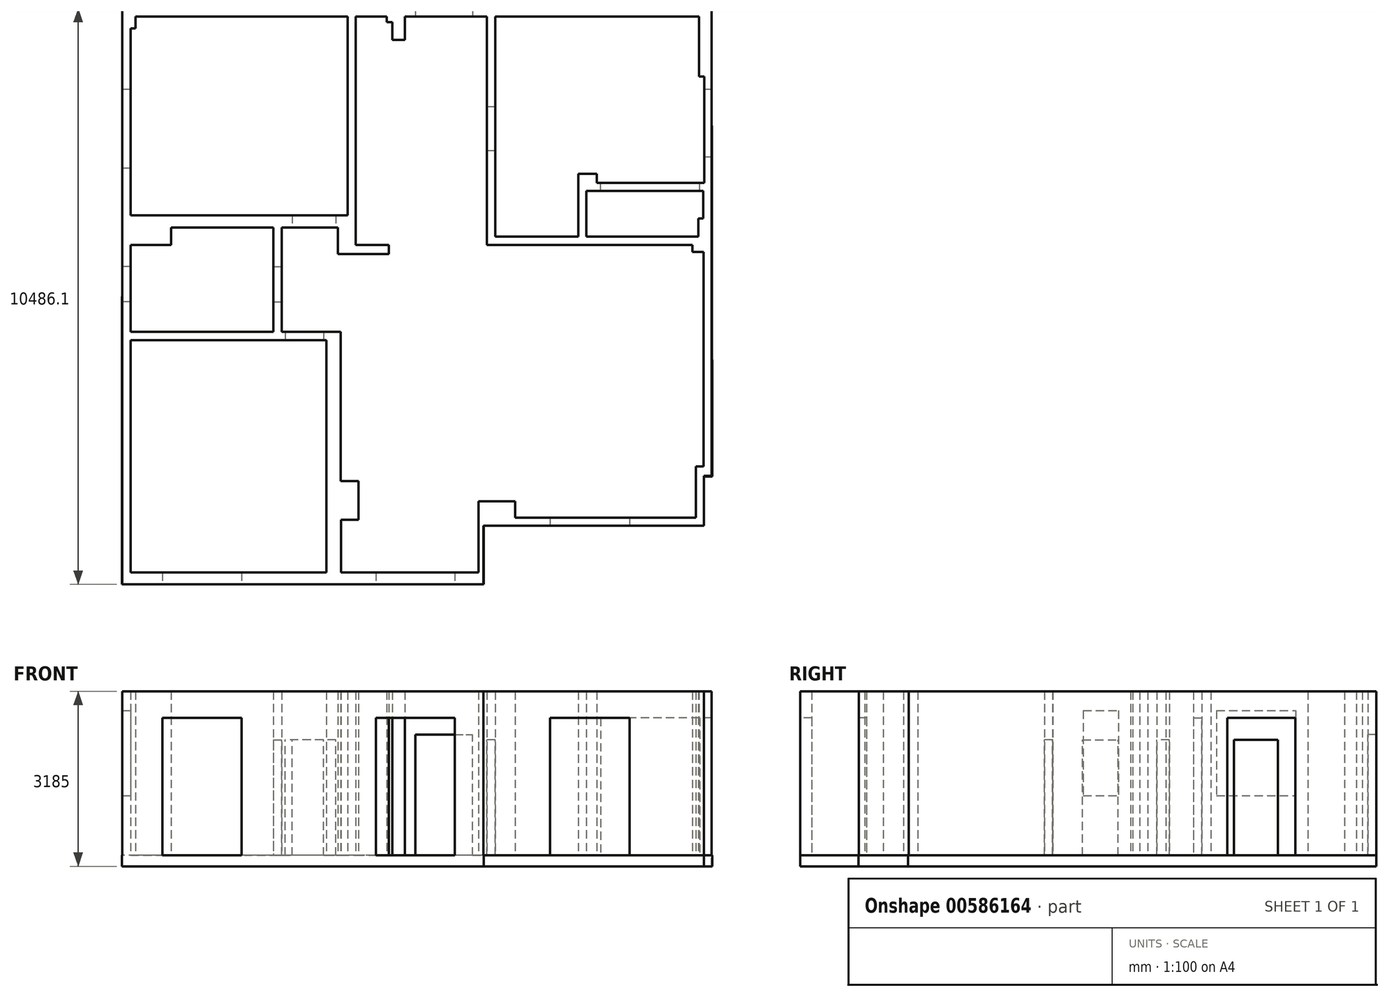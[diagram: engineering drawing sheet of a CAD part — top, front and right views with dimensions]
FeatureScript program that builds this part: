
annotation { "Feature Type Name" : "Feature", "Feature Type Description" : "" }
export const myFeature = defineFeature(function(context is Context, id is Id, definition is map)
    precondition{}
    {
        {
            var Q0;
            Q0=qCreatedBy(makeId("Top.planeOp"),FACE);
            var sketch = newSketch(context, id + "F0", { "sketchPlane" : qUnion([Q0])});
            skLineSegment(sketch, "E0", {"start": v(264.38, 0) * mm, "end": v(4001, 0) * mm});
            skLineSegment(sketch, "E1", {"start": v(4001, 0) * mm, "end": v(4001, -125) * mm});
            skLineSegment(sketch, "E2", {"start": v(4001, -125) * mm, "end": v(4202.95, -125) * mm});
            skLineSegment(sketch, "E3", {"start": v(4202.95, -125) * mm, "end": v(4202.95, -4036) * mm});
            skLineSegment(sketch, "E4", {"start": v(4202.95, -4036) * mm, "end": v(4062.95, -4036) * mm});
            skLineSegment(sketch, "E5", {"start": v(4062.95, -4036) * mm, "end": v(4062.95, -4967) * mm});
            skLineSegment(sketch, "E6", {"start": v(4062.95, -4967) * mm, "end": v(2970.95, -4967) * mm});
            skLineSegment(sketch, "E7", {"start": v(2970.95, -4967) * mm, "end": v(1520.95, -4967) * mm});
            skLineSegment(sketch, "E8", {"start": v(1520.95, -4967) * mm, "end": v(778.95, -4967) * mm});
            skLineSegment(sketch, "E9", {"start": v(778.95, -4967) * mm, "end": v(778.95, -4667) * mm});
            skLineSegment(sketch, "E10", {"start": v(778.95, -4667) * mm, "end": v(106.95, -4667) * mm});
            skLineSegment(sketch, "E11", {"start": v(106.95, -4667) * mm, "end": v(106.95, -5966) * mm});
            skLineSegment(sketch, "E12", {"start": v(106.95, -5966) * mm, "end": v(-320.05, -5966) * mm});
            skLineSegment(sketch, "E13", {"start": v(-320.05, -5966) * mm, "end": v(-1760.05, -5966) * mm});
            skLineSegment(sketch, "E14", {"start": v(-1760.05, -5966) * mm, "end": v(-2394.05, -5966) * mm});
            skLineSegment(sketch, "E15", {"start": v(-2394.05, -5966) * mm, "end": v(-2394.05, -5002) * mm});
            skLineSegment(sketch, "E16", {"start": v(-2394.05, -5002) * mm, "end": v(-2075.05, -5002) * mm});
            skLineSegment(sketch, "E17", {"start": v(-2075.05, -5002) * mm, "end": v(-2075.05, -4297) * mm});
            skLineSegment(sketch, "E18", {"start": v(-2075.05, -4297) * mm, "end": v(-2399.05, -4297) * mm});
            skLineSegment(sketch, "E19", {"start": v(-2399.05, -4297) * mm, "end": v(-2399.05, -1583) * mm});
            skLineSegment(sketch, "E20.19", {"start": v(3945.9, -4961.9) * mm, "end": v(2859, -4961.9) * mm});
            skLineSegment(sketch, "E21.0", {"start": v(2800.47, -5111.9) * mm, "end": v(1350.47, -5111.9) * mm});
            skLineSegment(sketch, "E22.0", {"start": v(1409, -5111.9) * mm, "end": v(720.85, -5111.9) * mm});
            skLineSegment(sketch, "E23", {"start": v(720.85, -5111.9) * mm, "end": v(198.85, -5111.9) * mm});
            skLineSegment(sketch, "E24", {"start": v(198.85, -5111.9) * mm, "end": v(198.85, -6179.3) * mm});
            skLineSegment(sketch, "E25", {"start": v(-435.2, -6179.3) * mm, "end": v(198.85, -6179.3) * mm});
            skLineSegment(sketch, "E26", {"start": v(2800.47, -5111.9) * mm, "end": v(4212.95, -5111.9) * mm});
            skLineSegment(sketch, "E27", {"start": v(-435.2, -6179.3) * mm, "end": v(-1872, -6179.3) * mm});
            skLineSegment(sketch, "E28", {"start": v(-1872, -6179.3) * mm, "end": v(-2660.9, -6179.3) * mm});
            skLineSegment(sketch, "E29", {"start": v(-2660.9, -1733) * mm, "end": v(-2660.9, -5966) * mm});
            skLineSegment(sketch, "E30", {"start": v(-2660.9, -1583) * mm, "end": v(-2399.05, -1583) * mm});
            skLineSegment(sketch, "E31", {"start": v(-1227.62, 4156.8) * mm, "end": v(-1227.62, 3731.8) * mm});
            skLineSegment(sketch, "E32", {"start": v(-1227.62, 3731.8) * mm, "end": v(-1461.62, 3731.8) * mm});
            skLineSegment(sketch, "E33", {"start": v(-1461.62, 3731.8) * mm, "end": v(-1461.62, 4055.8) * mm});
            skLineSegment(sketch, "E34", {"start": v(-1461.62, 4055.8) * mm, "end": v(-1562.62, 4055.8) * mm});
            skLineSegment(sketch, "E35", {"start": v(-1562.62, 4055.8) * mm, "end": v(-1562.62, 4156.8) * mm});
            skLineSegment(sketch, "E36", {"start": v(-1562.62, 4156.8) * mm, "end": v(-2123.62, 4156.8) * mm});
            skLineSegment(sketch, "E37", {"start": v(-2123.62, 4156.8) * mm, "end": v(-2123.62, 150) * mm});
            skLineSegment(sketch, "E38", {"start": v(264.38, 4156.8) * mm, "end": v(264.38, 0) * mm});
            skLineSegment(sketch, "E39", {"start": v(-1227.62, 4156.8) * mm, "end": v(264.38, 4156.8) * mm});
            skLineSegment(sketch, "E40.0", {"start": v(4198.9, 479.37) * mm, "end": v(4198.9, 981.37) * mm});
            skLineSegment(sketch, "E41", {"start": v(4108.9, 479.37) * mm, "end": v(4108.9, 149.4) * mm});
            skLineSegment(sketch, "E42", {"start": v(4108.9, 479.37) * mm, "end": v(4198.9, 479.37) * mm});
            skLineSegment(sketch, "E43", {"start": v(2073.52, 981.37) * mm, "end": v(4198.9, 981.37) * mm});
            skLineSegment(sketch, "E44.0", {"start": v(2262.52, 1131.37) * mm, "end": v(4215.38, 1131.37) * mm});
            skLineSegment(sketch, "E45", {"start": v(2262.52, 1131.37) * mm, "end": v(2262.52, 1296.37) * mm});
            skLineSegment(sketch, "E46", {"start": v(2262.52, 1296.37) * mm, "end": v(1923.52, 1296.37) * mm});
            skLineSegment(sketch, "E47.0", {"start": v(414.38, 4156.8) * mm, "end": v(414.38, 1131.37) * mm});
            skLineSegment(sketch, "E48", {"start": v(-2273.62, 4306.8) * mm, "end": v(4352.95, 4306.8) * mm});
            skLineSegment(sketch, "E49", {"start": v(414.38, 4156.8) * mm, "end": v(4125.38, 4156.8) * mm});
            skLineSegment(sketch, "E50.trimOffspring", {"start": v(4125.38, 4156.8) * mm, "end": v(4125.38, 3063.8) * mm});
            skLineSegment(sketch, "E51", {"start": v(2259.9, 150) * mm, "end": v(2259.9, 149.78) * mm});
            skLineSegment(sketch, "E52", {"start": v(2073.52, 149.82) * mm, "end": v(4108.9, 149.4) * mm});
            skLineSegment(sketch, "E53.trimOffspring", {"start": v(414.38, 1131.37) * mm, "end": v(414.38, 150) * mm});
            skLineSegment(sketch, "E54", {"start": v(-2273.62, 4156.8) * mm, "end": v(-2273.62, 541.1) * mm});
            skLineSegment(sketch, "E55.trimOffspring", {"start": v(414.38, 150) * mm, "end": v(1923.52, 150) * mm});
            skLineSegment(sketch, "E56", {"start": v(-2123.62, 150) * mm, "end": v(-2123.62, 0) * mm});
            skLineSegment(sketch, "E57", {"start": v(-2123.62, -166) * mm, "end": v(-2448.62, -166) * mm});
            skLineSegment(sketch, "E58", {"start": v(-2448.62, -166) * mm, "end": v(-2448.62, 316) * mm});
            skLineSegment(sketch, "E59", {"start": v(-3472.9, 316) * mm, "end": v(-3472.9, -1579.32) * mm});
            skLineSegment(sketch, "E60", {"start": v(-2448.62, 316) * mm, "end": v(-3472.9, 316) * mm});
            skLineSegment(sketch, "E61", {"start": v(-3472.9, -1579.32) * mm, "end": v(-2660.9, -1583) * mm});
            skLineSegment(sketch, "E62", {"start": v(-3622.9, 541.1) * mm, "end": v(-2273.62, 541.1) * mm});
            skLineSegment(sketch, "E63", {"start": v(-3622.9, 316) * mm, "end": v(-3622.9, -1583) * mm});
            skLineSegment(sketch, "E64", {"start": v(-2660.9, -1733) * mm, "end": v(-6222.9, -1733) * mm});
            skLineSegment(sketch, "E65", {"start": v(-6222.9, -1733) * mm, "end": v(-6222.9, -5966) * mm});
            skLineSegment(sketch, "E66", {"start": v(-2394.05, -5966) * mm, "end": v(-6222.9, -5966) * mm});
            skLineSegment(sketch, "E67", {"start": v(-2660.9, -6179.3) * mm, "end": v(-6372.9, -6179.3) * mm});
            skLineSegment(sketch, "E68", {"start": v(-6372.9, 541.1) * mm, "end": v(-6372.9, -6179.3) * mm});
            skLineSegment(sketch, "E69", {"start": v(-3622.9, -1583) * mm, "end": v(-6222.9, -1583) * mm});
            skLineSegment(sketch, "E70", {"start": v(-6222.9, -1583) * mm, "end": v(-6222.9, 0) * mm});
            skLineSegment(sketch, "E71", {"start": v(-3622.9, 316) * mm, "end": v(-5487.9, 316) * mm});
            skLineSegment(sketch, "E72", {"start": v(-5487.9, 316) * mm, "end": v(-5487.9, 0) * mm});
            skLineSegment(sketch, "E73", {"start": v(-6222.9, 0) * mm, "end": v(-5487.9, 0) * mm});
            skLineSegment(sketch, "E74", {"start": v(-3622.9, 541.1) * mm, "end": v(-6222.9, 541.1) * mm});
            skLineSegment(sketch, "E75", {"start": v(-6372.9, 541.1) * mm, "end": v(-6372.9, 4306.8) * mm});
            skLineSegment(sketch, "E76", {"start": v(-2273.62, 4306.8) * mm, "end": v(-6372.9, 4306.8) * mm});
            skLineSegment(sketch, "E77", {"start": v(-6222.9, 541.1) * mm, "end": v(-6222.9, 3944.8) * mm});
            skLineSegment(sketch, "E78", {"start": v(-2273.62, 4156.8) * mm, "end": v(-6132.9, 4156.8) * mm});
            skLineSegment(sketch, "E79", {"start": v(-6132.9, 4156.8) * mm, "end": v(-6132.9, 3944.8) * mm});
            skLineSegment(sketch, "E80.trimOffspring", {"start": v(-6222.9, 3944.8) * mm, "end": v(-6132.9, 3944.8) * mm});
            skLineSegment(sketch, "E81", {"start": v(4125.38, 3063.8) * mm, "end": v(4215.38, 3063.8) * mm});
            skLineSegment(sketch, "E82", {"start": v(4215.38, 3063.8) * mm, "end": v(4215.38, 1131.37) * mm});
            skLineSegment(sketch, "E83", {"start": v(4352.95, 4306.8) * mm, "end": v(4352.95, -4204.43) * mm});
            skLineSegment(sketch, "E84", {"start": v(4212.95, -4204.43) * mm, "end": v(4212.95, -5111.9) * mm});
            skLineSegment(sketch, "E85.trimOffspring", {"start": v(4212.95, -4204.43) * mm, "end": v(4352.95, -4204.43) * mm});
            skLineSegment(sketch, "E86", {"start": v(-2123.62, -166) * mm, "end": v(-1523.62, -166) * mm});
            skLineSegment(sketch, "E87", {"start": v(-2123.62, 0) * mm, "end": v(-1523.62, 0) * mm});
            skLineSegment(sketch, "E88", {"start": v(-1523.62, -166) * mm, "end": v(-1523.62, 0) * mm});
            skLineSegment(sketch, "E89", {"start": v(1923.52, 1296.37) * mm, "end": v(1923.52, 150) * mm});
            skLineSegment(sketch, "E90", {"start": v(2073.52, 981.37) * mm, "end": v(2073.52, 145.98) * mm});
            skPoint(sketch, "E91.orphan", {"position": v(2259.9, 981.37) * mm});
            skLineSegment(sketch, "E92", {"start": v(4062.95, -4501.5) * mm, "end": v(912.95, -4501.5) * mm});
            skLineSegment(sketch, "E93", {"start": v(4062.95, -4501.5) * mm, "end": v(4062.95, -2701.5) * mm});
            skLineSegment(sketch, "E94", {"start": v(4062.95, -2701.5) * mm, "end": v(2945.08, -2701.5) * mm});
            skLineSegment(sketch, "E95", {"start": v(2945.08, -2701.5) * mm, "end": v(2945.08, -3501.5) * mm});
            skLineSegment(sketch, "E96", {"start": v(2945.08, -3501.5) * mm, "end": v(869.18, -3501.5) * mm});
            skLineSegment(sketch, "E97", {"start": v(869.18, -3501.5) * mm, "end": v(912.95, -4501.5) * mm});
            skSolve(sketch);
        }
        {
            var Q0;
            Q0=qSketchRegion(id+"F0",true);
            extrude(context, id + "F1", {"entities" : qUnion([Q0]), "depth" : 2985 * mm, "offsetDistance" : 25 * mm});
        }
        {
            var Q0;
            Q0=makeQuery(id+"F1.opExtrude","SWEPT_FACE",FACE,{"disambiguationData":[OSD([sQuery(id+"F0.wireOp",EDGE,"E21.0"),sQuery(id+"F0.wireOp",EDGE,"E22.0"),sQuery(id+"F0.wireOp",EDGE,"E23"),sQuery(id+"F0.wireOp",EDGE,"E26")])]});
            var sketch = newSketch(context, id + "F2", { "sketchPlane" : qUnion([Q0])});
            skLineSegment(sketch, "E98.bottom", {"start": v(2859, 0) * mm, "end": v(1409, 0) * mm});
            skLineSegment(sketch, "E98.top", {"start": v(2859, 2500) * mm, "end": v(1409, 2500) * mm});
            skLineSegment(sketch, "E98.left", {"start": v(2859, 0) * mm, "end": v(2859, 2500) * mm});
            skLineSegment(sketch, "E98.right", {"start": v(1409, 0) * mm, "end": v(1409, 2500) * mm});
            skSolve(sketch);
        }
        {
            var Q0;
            Q0=qSketchRegion(id+"F2",true);
            extrude(context, id + "F3", {"entities" : qUnion([Q0]), "operationType" : NewBodyOperationType.REMOVE, "endBound" : BoundingType.UP_TO_NEXT, "oppositeDirection" : true, "depth" : 25 * mm, "offsetDistance" : 25 * mm});
        }
        {
            var Q0;
            Q0=makeQuery(id+"F1.opExtrude","SWEPT_FACE",FACE,{"disambiguationData":[OSD([sQuery(id+"F0.wireOp",EDGE,"E25"),sQuery(id+"F0.wireOp",EDGE,"E27"),sQuery(id+"F0.wireOp",EDGE,"E28"),sQuery(id+"F0.wireOp",EDGE,"E67")])]});
            var sketch = newSketch(context, id + "F4", { "sketchPlane" : qUnion([Q0])});
            skLineSegment(sketch, "E99.bottom", {"start": v(-320.05, 0) * mm, "end": v(-1760.05, 0) * mm});
            skLineSegment(sketch, "E99.top", {"start": v(-320.05, 2500) * mm, "end": v(-1760.05, 2500) * mm});
            skLineSegment(sketch, "E99.left", {"start": v(-320.05, 0) * mm, "end": v(-320.05, 2500) * mm});
            skLineSegment(sketch, "E99.right", {"start": v(-1760.05, 0) * mm, "end": v(-1760.05, 2500) * mm});
            skSolve(sketch);
        }
        {
            var Q0;
            Q0=qSketchRegion(id+"F4",true);
            extrude(context, id + "F5", {"entities" : qUnion([Q0]), "operationType" : NewBodyOperationType.REMOVE, "endBound" : BoundingType.UP_TO_NEXT, "oppositeDirection" : true, "depth" : 25 * mm, "offsetDistance" : 25 * mm});
        }
        {
            var Q0;
            Q0=makeQuery(id+"F1.opExtrude","SWEPT_FACE",FACE,{"disambiguationData":[OSD([sQuery(id+"F0.wireOp",EDGE,"E25"),sQuery(id+"F0.wireOp",EDGE,"E27"),sQuery(id+"F0.wireOp",EDGE,"E28"),sQuery(id+"F0.wireOp",EDGE,"E67")])]});
            var sketch = newSketch(context, id + "F6", { "sketchPlane" : qUnion([Q0])});
            skLineSegment(sketch, "E100.bottom", {"start": v(-4201.9, 0) * mm, "end": v(-5644.9, 0) * mm});
            skLineSegment(sketch, "E100.top", {"start": v(-4201.9, 2500) * mm, "end": v(-5644.9, 2500) * mm});
            skLineSegment(sketch, "E100.left", {"start": v(-4201.9, 0) * mm, "end": v(-4201.9, 2500) * mm});
            skLineSegment(sketch, "E100.right", {"start": v(-5644.9, 0) * mm, "end": v(-5644.9, 2500) * mm});
            skSolve(sketch);
        }
        {
            var Q0;
            Q0=qSketchRegion(id+"F6",true);
            extrude(context, id + "F7", {"entities" : qUnion([Q0]), "operationType" : NewBodyOperationType.REMOVE, "endBound" : BoundingType.UP_TO_NEXT, "oppositeDirection" : true, "depth" : 25 * mm, "offsetDistance" : 25 * mm});
        }
        {
            var Q0;
            Q0=makeQuery(id+"F1.opExtrude","SWEPT_FACE",FACE,{"disambiguationData":[OSD([sQuery(id+"F0.wireOp",EDGE,"E0"),sQuery(id+"F0.wireOp",EDGE,"s7OnHrYy-Djpp-lhPn-glBJ-n8gcuGNVqWHS"),sQuery(id+"F0.wireOp",EDGE,"TmqLxYyP-QGwx-pu5G-LCv3-DPf7TJavojwj")])]});
            var sketch = newSketch(context, id + "F8", { "sketchPlane" : qUnion([Q0])});
            skLineSegment(sketch, "E101.bottom", {"start": v(0, 0) * mm, "end": v(-797, 0) * mm});
            skLineSegment(sketch, "E101.top", {"start": v(0, 2500) * mm, "end": v(-797, 2500) * mm});
            skLineSegment(sketch, "E101.left", {"start": v(0, 0) * mm, "end": v(0, 2500) * mm});
            skLineSegment(sketch, "E101.right", {"start": v(-797, 0) * mm, "end": v(-797, 2500) * mm});
            skSolve(sketch);
        }
        {
            var Q0;
            Q0=qSketchRegion(id+"F8",true);
            extrude(context, id + "F9", {"entities" : qUnion([Q0]), "operationType" : NewBodyOperationType.REMOVE, "endBound" : BoundingType.UP_TO_NEXT, "oppositeDirection" : true, "depth" : 25 * mm, "offsetDistance" : 25 * mm});
        }
        {
            var Q0;
            Q0=makeQuery(id+"F1.opExtrude","SWEPT_FACE",FACE,{"disambiguationData":[OSD([sQuery(id+"F0.wireOp",EDGE,"E38")])]});
            var sketch = newSketch(context, id + "F10", { "sketchPlane" : qUnion([Q0])});
            skLineSegment(sketch, "E102.bottom", {"start": v(-1715.5, 0) * mm, "end": v(-2515.5, 0) * mm});
            skLineSegment(sketch, "E102.top", {"start": v(-1715.5, 2100) * mm, "end": v(-2515.5, 2100) * mm});
            skLineSegment(sketch, "E102.left", {"start": v(-1715.5, 0) * mm, "end": v(-1715.5, 2100) * mm});
            skLineSegment(sketch, "E102.right", {"start": v(-2515.5, 0) * mm, "end": v(-2515.5, 2100) * mm});
            skSolve(sketch);
        }
        {
            var Q0;
            Q0=qSketchRegion(id+"F10",true);
            extrude(context, id + "F11", {"entities" : qUnion([Q0]), "operationType" : NewBodyOperationType.REMOVE, "endBound" : BoundingType.UP_TO_NEXT, "oppositeDirection" : true, "depth" : 25 * mm, "offsetDistance" : 25 * mm});
        }
        {
            var Q0;
            Q0=makeQuery(id+"F1.opExtrude","SWEPT_FACE",FACE,{"disambiguationData":[OSD([sQuery(id+"F0.wireOp",EDGE,"E39")])]});
            var sketch = newSketch(context, id + "F12", { "sketchPlane" : qUnion([Q0])});
            skLineSegment(sketch, "E103.bottom", {"start": v(-1042, 0) * mm, "end": v(0, 0) * mm});
            skLineSegment(sketch, "E103.top", {"start": v(-1042, 2200) * mm, "end": v(0, 2200) * mm});
            skLineSegment(sketch, "E103.left", {"start": v(-1042, 0) * mm, "end": v(-1042, 2200) * mm});
            skLineSegment(sketch, "E103.right", {"start": v(0, 0) * mm, "end": v(0, 2200) * mm});
            skSolve(sketch);
        }
        {
            var Q0;
            Q0=qSketchRegion(id+"F12",true);
            extrude(context, id + "F13", {"entities" : qUnion([Q0]), "operationType" : NewBodyOperationType.REMOVE, "endBound" : BoundingType.UP_TO_NEXT, "oppositeDirection" : true, "depth" : 25 * mm, "offsetDistance" : 25 * mm});
        }
        {
            var Q0;
            Q0=makeQuery(id+"F1.opExtrude","SWEPT_FACE",FACE,{"disambiguationData":[OSD([sQuery(id+"F0.wireOp",EDGE,"E82")])]});
            var sketch = newSketch(context, id + "F14", { "sketchPlane" : qUnion([Q0])});
            skLineSegment(sketch, "E104.bottom", {"start": v(-2833.8, 0) * mm, "end": v(-1598.8, 0) * mm});
            skLineSegment(sketch, "E104.top", {"start": v(-2833.8, 2500) * mm, "end": v(-1598.8, 2500) * mm});
            skLineSegment(sketch, "E104.left", {"start": v(-2833.8, 0) * mm, "end": v(-2833.8, 2500) * mm});
            skLineSegment(sketch, "E104.right", {"start": v(-1598.8, 0) * mm, "end": v(-1598.8, 2500) * mm});
            skSolve(sketch);
        }
        {
            var Q0;
            Q0=qSketchRegion(id+"F14",true);
            extrude(context, id + "F15", {"entities" : qUnion([Q0]), "operationType" : NewBodyOperationType.REMOVE, "endBound" : BoundingType.UP_TO_NEXT, "oppositeDirection" : true, "depth" : 25 * mm, "offsetDistance" : 25 * mm});
        }
        {
            var Q0;
            Q0=makeQuery(id+"F1.opExtrude","SWEPT_FACE",FACE,{"disambiguationData":[OSD([sQuery(id+"F0.wireOp",EDGE,"E64")])]});
            var sketch = newSketch(context, id + "F16", { "sketchPlane" : qUnion([Q0])});
            skLineSegment(sketch, "E105.bottom", {"start": v(-2710.9, 0) * mm, "end": v(-3410.9, 0) * mm});
            skLineSegment(sketch, "E105.top", {"start": v(-2710.9, 2100) * mm, "end": v(-3410.9, 2100) * mm});
            skLineSegment(sketch, "E105.left", {"start": v(-2710.9, 0) * mm, "end": v(-2710.9, 2100) * mm});
            skLineSegment(sketch, "E105.right", {"start": v(-3410.9, 0) * mm, "end": v(-3410.9, 2100) * mm});
            skSolve(sketch);
        }
        {
            var Q0;
            Q0=qSketchRegion(id+"F16",true);
            extrude(context, id + "F17", {"entities" : qUnion([Q0]), "operationType" : NewBodyOperationType.REMOVE, "endBound" : BoundingType.UP_TO_NEXT, "oppositeDirection" : true, "depth" : 25 * mm, "offsetDistance" : 25 * mm});
        }
        {
            var Q0;
            Q0=makeQuery(id+"F1.opExtrude","SWEPT_FACE",FACE,{"disambiguationData":[OSD([sQuery(id+"F0.wireOp",EDGE,"E60")])]});
            var sketch = newSketch(context, id + "F18", { "sketchPlane" : qUnion([Q0])});
            skLineSegment(sketch, "E106.bottom", {"start": v(-2488.9, 0) * mm, "end": v(-3282.9, 0) * mm});
            skLineSegment(sketch, "E106.top", {"start": v(-2488.9, 2100) * mm, "end": v(-3282.9, 2100) * mm});
            skLineSegment(sketch, "E106.left", {"start": v(-2488.9, 0) * mm, "end": v(-2488.9, 2100) * mm});
            skLineSegment(sketch, "E106.right", {"start": v(-3282.9, 0) * mm, "end": v(-3282.9, 2100) * mm});
            skSolve(sketch);
        }
        {
            var Q0;
            Q0=qSketchRegion(id+"F18",true);
            extrude(context, id + "F19", {"entities" : qUnion([Q0]), "operationType" : NewBodyOperationType.REMOVE, "endBound" : BoundingType.UP_TO_NEXT, "oppositeDirection" : true, "depth" : 25 * mm, "offsetDistance" : 25 * mm});
        }
        {
            var Q0;
            Q0=makeQuery(id+"F1.opExtrude","SWEPT_FACE",FACE,{"disambiguationData":[OSD([sQuery(id+"F0.wireOp",EDGE,"E59")])]});
            var sketch = newSketch(context, id + "F20", { "sketchPlane" : qUnion([Q0])});
            skLineSegment(sketch, "E107.bottom", {"start": v(-1039, 0) * mm, "end": v(-393, 0) * mm});
            skLineSegment(sketch, "E107.top", {"start": v(-1039, 2100) * mm, "end": v(-393, 2100) * mm});
            skLineSegment(sketch, "E107.left", {"start": v(-1039, 0) * mm, "end": v(-1039, 2100) * mm});
            skLineSegment(sketch, "E107.right", {"start": v(-393, 0) * mm, "end": v(-393, 2100) * mm});
            skSolve(sketch);
        }
        {
            var Q0;
            Q0=qSketchRegion(id+"F20",true);
            extrude(context, id + "F21", {"entities" : qUnion([Q0]), "operationType" : NewBodyOperationType.REMOVE, "endBound" : BoundingType.UP_TO_NEXT, "oppositeDirection" : true, "depth" : 25 * mm, "offsetDistance" : 25 * mm});
        }
        {
            var Q0;
            Q0=makeQuery(id+"F1.opExtrude","SWEPT_FACE",FACE,{"disambiguationData":[OSD([sQuery(id+"F0.wireOp",EDGE,"E70")])]});
            var sketch = newSketch(context, id + "F22", { "sketchPlane" : qUnion([Q0])});
            skLineSegment(sketch, "E108.bottom", {"start": v(-1027.15, 2635) * mm, "end": v(-387.15, 2635) * mm});
            skLineSegment(sketch, "E108.top", {"start": v(-1027.15, 1085) * mm, "end": v(-387.15, 1085) * mm});
            skLineSegment(sketch, "E108.left", {"start": v(-1027.15, 2635) * mm, "end": v(-1027.15, 1085) * mm});
            skLineSegment(sketch, "E108.right", {"start": v(-387.15, 2635) * mm, "end": v(-387.15, 1085) * mm});
            skSolve(sketch);
        }
        {
            var Q0;
            Q0=qSketchRegion(id+"F22",true);
            extrude(context, id + "F23", {"entities" : qUnion([Q0]), "operationType" : NewBodyOperationType.REMOVE, "endBound" : BoundingType.UP_TO_NEXT, "oppositeDirection" : true, "depth" : 25 * mm, "offsetDistance" : 25 * mm});
        }
        {
            var Q0;
            Q0=makeQuery(id+"F1.opExtrude","SWEPT_FACE",FACE,{"disambiguationData":[OSD([sQuery(id+"F0.wireOp",EDGE,"E77")])]});
            var sketch = newSketch(context, id + "F24", { "sketchPlane" : qUnion([Q0])});
            skLineSegment(sketch, "E109.bottom", {"start": v(1400.8, 2635) * mm, "end": v(2838.8, 2635) * mm});
            skLineSegment(sketch, "E109.top", {"start": v(1400.8, 1085) * mm, "end": v(2838.8, 1085) * mm});
            skLineSegment(sketch, "E109.left", {"start": v(1400.8, 2635) * mm, "end": v(1400.8, 1085) * mm});
            skLineSegment(sketch, "E109.right", {"start": v(2838.8, 2635) * mm, "end": v(2838.8, 1085) * mm});
            skSolve(sketch);
        }
        {
            var Q0;
            Q0=qSketchRegion(id+"F24",true);
            extrude(context, id + "F25", {"entities" : qUnion([Q0]), "operationType" : NewBodyOperationType.REMOVE, "endBound" : BoundingType.UP_TO_NEXT, "oppositeDirection" : true, "depth" : 25 * mm, "offsetDistance" : 25 * mm});
        }
        {
            var Q0;
            {var subQ1=sQuery(id+"F0.wireOp",EDGE,"SHYwI1Km-nGdX-hWiI-bBXE-USSKnqkYGS6a");var subQ5=sQuery(id+"F0.wireOp",EDGE,"E16");var subQ7=sQuery(id+"F0.wireOp",EDGE,"E61");var subQ9=sQuery(id+"F0.wireOp",EDGE,"E66");var subQ11=sQuery(id+"F0.wireOp",EDGE,"YjNxKa04-D713-GkI1-3dHD-v2EvdFtaiUNy");var subQ12=sQuery(id+"F0.wireOp",EDGE,"Pk8GRUs5-Ct7U-xnJC-PrK4-SelXqmJglOKg");var subQ13=sQuery(id+"F0.wireOp",EDGE,"43ddc9e9-362d-4df6-b2eb-0e09625f2240.0");var subQ15=sQuery(id+"F0.wireOp",EDGE,"E29");var subQ17=sQuery(id+"F0.wireOp",EDGE,"E67");var subQ18=sQuery(id+"F0.wireOp",EDGE,"E28");var subQ19=sQuery(id+"F0.wireOp",EDGE,"E27");var subQ20=sQuery(id+"F0.wireOp",EDGE,"E25");var subQ22=sQuery(id+"F0.wireOp",EDGE,"E15");var subQ23=makeQuery(id+"F1.opExtrude","SWEPT_FACE",FACE,{"disambiguationData":[OSD([subQ22])]});var subQ24=sQuery(id+"F0.wireOp",EDGE,"E30");var subQ26=sQuery(id+"F0.wireOp",EDGE,"TmqLxYyP-QGwx-pu5G-LCv3-DPf7TJavojwj");var subQ27=sQuery(id+"F0.wireOp",EDGE,"s7OnHrYy-Djpp-lhPn-glBJ-n8gcuGNVqWHS");var subQ28=sQuery(id+"F0.wireOp",EDGE,"E0");var subQ30=sQuery(id+"F0.wireOp",EDGE,"E14");var subQ31=sQuery(id+"F0.wireOp",EDGE,"E13");var subQ32=sQuery(id+"F0.wireOp",EDGE,"E12");var subQ34=sQuery(id+"F0.wireOp",EDGE,"E17");var subQ36=sQuery(id+"F0.wireOp",EDGE,"E18");var subQ39=sQuery(id+"F0.wireOp",EDGE,"eoeD3Byo-P0gw-txBY-vvlC-kslMNdlaTYqU");var subQ41=sQuery(id+"F0.wireOp",EDGE,"E19");var subQ43=sQuery(id+"F0.wireOp",EDGE,"72bfnt6n-2u4T-0vj5-kmEr-8OWYGDq4sTvC");var subQ45=sQuery(id+"F0.wireOp",EDGE,"BhLDGgfD-mt54-uttg-1J56-lKjsMIqC0sHZ");var subQ47=sQuery(id+"F0.wireOp",EDGE,"E64");var subQ49=sQuery(id+"F0.wireOp",EDGE,"E69");var subQ51=sQuery(id+"F0.wireOp",EDGE,"E75");var subQ52=sQuery(id+"F0.wireOp",EDGE,"E68");var subQ54=sQuery(id+"F0.wireOp",EDGE,"E58");var subQ56=sQuery(id+"F0.wireOp",EDGE,"E57");var subQ58=sQuery(id+"F0.wireOp",EDGE,"E56");var subQ60=sQuery(id+"F0.wireOp",EDGE,"E54");var subQ62=sQuery(id+"F0.wireOp",EDGE,"E76");var subQ63=sQuery(id+"F0.wireOp",EDGE,"E48");var subQ65=sQuery(id+"F0.wireOp",EDGE,"E65");var subQ67=sQuery(id+"F0.wireOp",EDGE,"E63");var subQ69=sQuery(id+"F0.wireOp",EDGE,"E74");var subQ70=sQuery(id+"F0.wireOp",EDGE,"E62");var subQ72=sQuery(id+"F0.wireOp",EDGE,"E59");var subQ74=sQuery(id+"F0.wireOp",EDGE,"E39");var subQ76=sQuery(id+"F0.wireOp",EDGE,"E72");var subQ78=sQuery(id+"F0.wireOp",EDGE,"E60");var subQ80=sQuery(id+"F0.wireOp",EDGE,"E70");var subQ82=sQuery(id+"F0.wireOp",EDGE,"E71");var subQ84=sQuery(id+"F0.wireOp",EDGE,"E73");var subQ86=sQuery(id+"F0.wireOp",EDGE,"E77");var subQ88=sQuery(id+"F0.wireOp",EDGE,"E31");var subQ90=sQuery(id+"F0.wireOp",EDGE,"E78");var subQ92=sQuery(id+"F0.wireOp",EDGE,"E32");var subQ94=sQuery(id+"F0.wireOp",EDGE,"E79");var subQ96=sQuery(id+"F0.wireOp",EDGE,"E33");var subQ98=sQuery(id+"F0.wireOp",EDGE,"E80.trimOffspring");var subQ100=sQuery(id+"F0.wireOp",EDGE,"E34");var subQ102=sQuery(id+"F0.wireOp",EDGE,"E35");var subQ104=sQuery(id+"F0.wireOp",EDGE,"E36");var subQ106=sQuery(id+"F0.wireOp",EDGE,"E37");var subQ108=sQuery(id+"F0.wireOp",EDGE,"cf3721b8-3da9-4641-a597-ca2e7abb297d");var subQ109=sQuery(id+"F0.wireOp",EDGE,"E50.trimOffspring");var subQ110=sQuery(id+"F0.wireOp",EDGE,"E49");var subQ111=sQuery(id+"F0.wireOp",EDGE,"E47.0");var subQ112=sQuery(id+"F0.wireOp",EDGE,"2b54ef7b-5aee-4bcd-ac23-5266368806b8");var subQ113=sQuery(id+"F0.wireOp",EDGE,"E46");var subQ114=sQuery(id+"F0.wireOp",EDGE,"E45");var subQ115=sQuery(id+"F0.wireOp",EDGE,"E44.0");var subQ116=sQuery(id+"F0.wireOp",EDGE,"E43");var subQ117=sQuery(id+"F0.wireOp",EDGE,"E42");var subQ118=sQuery(id+"F0.wireOp",EDGE,"E41");var subQ119=sQuery(id+"F0.wireOp",EDGE,"E40.0");var subQ120=sQuery(id+"F0.wireOp",EDGE,"E38");var subQ121=sQuery(id+"F0.wireOp",EDGE,"E8");var subQ122=sQuery(id+"F0.wireOp",EDGE,"E7");var subQ123=sQuery(id+"F0.wireOp",EDGE,"E6");var subQ124=sQuery(id+"F0.wireOp",EDGE,"E5");var subQ125=sQuery(id+"F0.wireOp",EDGE,"E4");var subQ126=sQuery(id+"F0.wireOp",EDGE,"E51");var subQ127=sQuery(id+"F0.wireOp",EDGE,"E52");var subQ128=sQuery(id+"F0.wireOp",EDGE,"E1");var subQ129=sQuery(id+"F0.wireOp",EDGE,"d12652c7-2e03-49a7-b153-276cc3c063a4.0");var subQ130=sQuery(id+"F0.wireOp",EDGE,"E2");var subQ131=sQuery(id+"F0.wireOp",EDGE,"E3");var subQ132=sQuery(id+"F0.wireOp",EDGE,"E26");var subQ133=sQuery(id+"F0.wireOp",EDGE,"E23");var subQ134=sQuery(id+"F0.wireOp",EDGE,"E22.0");var subQ135=sQuery(id+"F0.wireOp",EDGE,"E21.0");var subQ136=sQuery(id+"F0.wireOp",EDGE,"69339179-5628-4f70-9663-4bc6529cb7e1");var subQ137=sQuery(id+"F0.wireOp",EDGE,"E53.trimOffspring");var subQ138=sQuery(id+"F0.wireOp",EDGE,"E55.trimOffspring");var subQ139=sQuery(id+"F0.wireOp",EDGE,"E81");var subQ140=sQuery(id+"F0.wireOp",EDGE,"E82");var subQ141=sQuery(id+"F0.wireOp",EDGE,"E83");var subQ142=sQuery(id+"F0.wireOp",EDGE,"E84");var subQ143=sQuery(id+"F0.wireOp",EDGE,"E85.trimOffspring");Q0=makeQuery(id+"F928qljx548FBxZ_1.boolean.opBoolean","SPLIT",FACE,{"disambiguationData":[TD([subQ23])],"derivedFrom":makeQuery(id+"F13.boolean.opBoolean","SPLIT",FACE,{"disambiguationData":[TD([subQ23])],"derivedFrom":makeQuery(id+"F5.boolean.opBoolean","SPLIT",FACE,{"disambiguationData":[TD([makeQuery(id+"F1.opExtrude","SWEPT_FACE",FACE,{"disambiguationData":[OSD([subQ128])]})])],"derivedFrom":makeQuery(id+"F1.opExtrude","CAP_FACE",FACE,{"disambiguationData":[OSD([subQ28,subQ128,subQ130,subQ131,subQ125,subQ124,subQ123,subQ122,subQ121,subQ27,sQuery(id+"F0.wireOp",EDGE,"E9"),sQuery(id+"F0.wireOp",EDGE,"E10"),sQuery(id+"F0.wireOp",EDGE,"E11"),subQ32,subQ31,subQ30,subQ22,subQ5,subQ34,subQ36,subQ41,subQ26,subQ45,subQ39,subQ13,subQ135,subQ134,subQ133,sQuery(id+"F0.wireOp",EDGE,"E24"),subQ20,subQ132,subQ19,subQ18,subQ15,subQ24,subQ1,subQ12,subQ88,subQ92,subQ96,subQ100,subQ102,subQ104,subQ106,subQ120,subQ74,subQ119,subQ118,subQ117,subQ116,subQ115,subQ114,subQ113,subQ112,subQ111,subQ63,subQ110,subQ109,subQ108,subQ126,subQ127,subQ129,subQ136,subQ137,subQ60,subQ138,subQ11,subQ58,subQ56,subQ54,subQ72,subQ78,subQ7,subQ70,subQ67,subQ43,subQ47,subQ65,subQ9,subQ17,subQ52,subQ49,subQ80,subQ82,subQ76,subQ84,subQ69,subQ51,subQ62,subQ86,subQ90,subQ94,subQ98,subQ139,subQ140,subQ141,subQ142,subQ143])],"isStart":true})})})});}
            var sketch = newSketch(context, id + "F26", { "sketchPlane" : qUnion([Q0])});
            skLineSegment(sketch, "E110", {"start": v(-6377.03, 6179.3) * mm, "end": v(202.74, 6179.3) * mm});
            skLineSegment(sketch, "E111", {"start": v(202.74, 6179.3) * mm, "end": v(202.74, 5115.2) * mm});
            skLineSegment(sketch, "E112", {"start": v(202.74, 5115.2) * mm, "end": v(4213.98, 5115.2) * mm});
            skLineSegment(sketch, "E113", {"start": v(4213.98, 5115.2) * mm, "end": v(4213.98, 4216.05) * mm});
            skLineSegment(sketch, "E114", {"start": v(4213.98, 4216.05) * mm, "end": v(4361.62, 4216.05) * mm});
            skLineSegment(sketch, "E115", {"start": v(4361.62, 4216.05) * mm, "end": v(4353.72, -4305.73) * mm});
            skLineSegment(sketch, "E116", {"start": v(4353.72, -4305.73) * mm, "end": v(-6373.4, -4305.73) * mm});
            skLineSegment(sketch, "E117", {"start": v(-6373.4, -4305.73) * mm, "end": v(-6377.03, 6179.3) * mm});
            skSolve(sketch);
        }
        {
            var Q0;
            Q0=qSketchRegion(id+"F26",true);
            extrude(context, id + "F27", {"entities" : qUnion([Q0]), "operationType" : NewBodyOperationType.ADD, "depth" : 200 * mm, "offsetDistance" : 25 * mm});
        }
        {
            var Q0;
            Q0=makeQuery(id+"F1.opExtrude","SWEPT_FACE",FACE,{"disambiguationData":[OSD([sQuery(id+"F0.wireOp",EDGE,"E44.0")])]});
            var sketch = newSketch(context, id + "F28", { "sketchPlane" : qUnion([Q0])});
            skLineSegment(sketch, "E118.bottom", {"start": v(-2332.52, 0) * mm, "end": v(-4132.52, 0) * mm});
            skLineSegment(sketch, "E118.top", {"start": v(-2332.52, 2500) * mm, "end": v(-4132.52, 2500) * mm});
            skLineSegment(sketch, "E118.left", {"start": v(-2332.52, 0) * mm, "end": v(-2332.52, 2500) * mm});
            skLineSegment(sketch, "E118.right", {"start": v(-4132.52, 0) * mm, "end": v(-4132.52, 2500) * mm});
            skSolve(sketch);
        }
        {
            var Q0;
            Q0 = qSketchRegion(id + "F28", true);
            extrude(context, id + "F29", {"entities" : qUnion([Q0]), "operationType" : NewBodyOperationType.REMOVE, "endBound" : BoundingType.UP_TO_NEXT, "oppositeDirection" : true, "depth" : 25 * mm, "offsetDistance" : 25 * mm});
        }
    });
